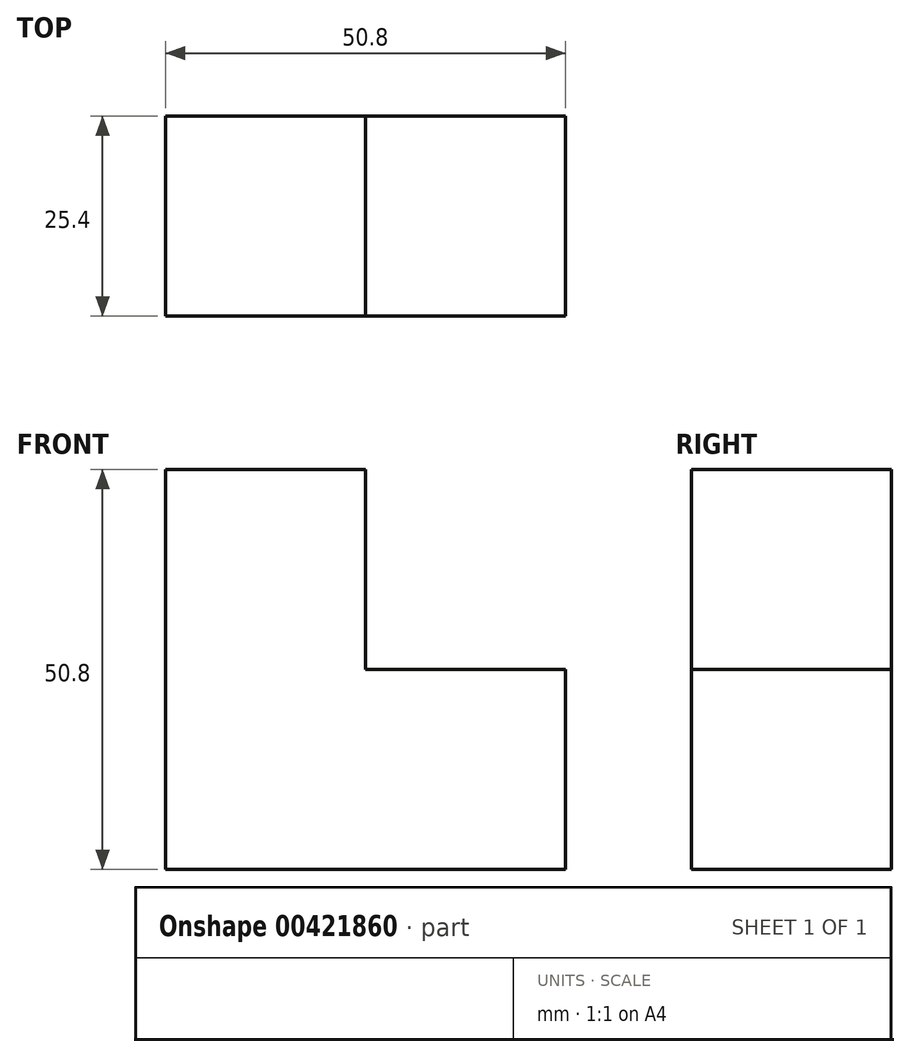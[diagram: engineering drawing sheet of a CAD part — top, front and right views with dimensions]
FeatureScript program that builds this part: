
annotation { "Feature Type Name" : "Feature", "Feature Type Description" : "" }
export const myFeature = defineFeature(function(context is Context, id is Id, definition is map)
    precondition{}
    {
        {
            var Q0;
            Q0=qCreatedBy(makeId("Front.planeOp"),FACE);
            var sketch = newSketch(context, id + "F0", { "sketchPlane" : qUnion([Q0])});
            skLineSegment(sketch, "E0", {"start": v(0, 0) * mm, "end": v(-50.8, 0) * mm});
            skLineSegment(sketch, "E1", {"start": v(-50.8, 0) * mm, "end": v(-50.8, 50.8) * mm});
            skLineSegment(sketch, "E2", {"start": v(-50.8, 50.8) * mm, "end": v(-25.4, 50.8) * mm});
            skLineSegment(sketch, "E3", {"start": v(-25.4, 50.8) * mm, "end": v(-25.4, 25.4) * mm});
            skLineSegment(sketch, "E4", {"start": v(-25.4, 25.4) * mm, "end": v(0, 25.4) * mm});
            skLineSegment(sketch, "E5", {"start": v(0, 25.4) * mm, "end": v(0, 0) * mm});
            skArc(sketch, "E6", {"start": v(-25.4, 50.8) * mm, "mid": v(-16.74, 34.06) * mm, "end": v(0, 25.4) * mm});
            skSolve(sketch);
        }
        {
            var Q0;
            Q0=makeQuery(id+"F0.imprint","IMPRINT",FACE,{"disambiguationData":[TD([[makeQuery(id+"F0.imprint","IMPRINT",EDGE,{"derivedFrom":sQuery(id+"F0.wireOp",EDGE,"E0")}),-1.0]])]});
            extrude(context, id + "F1", {"entities" : qUnion([Q0]), "depth" : 25.4 * mm});
        }
    });
